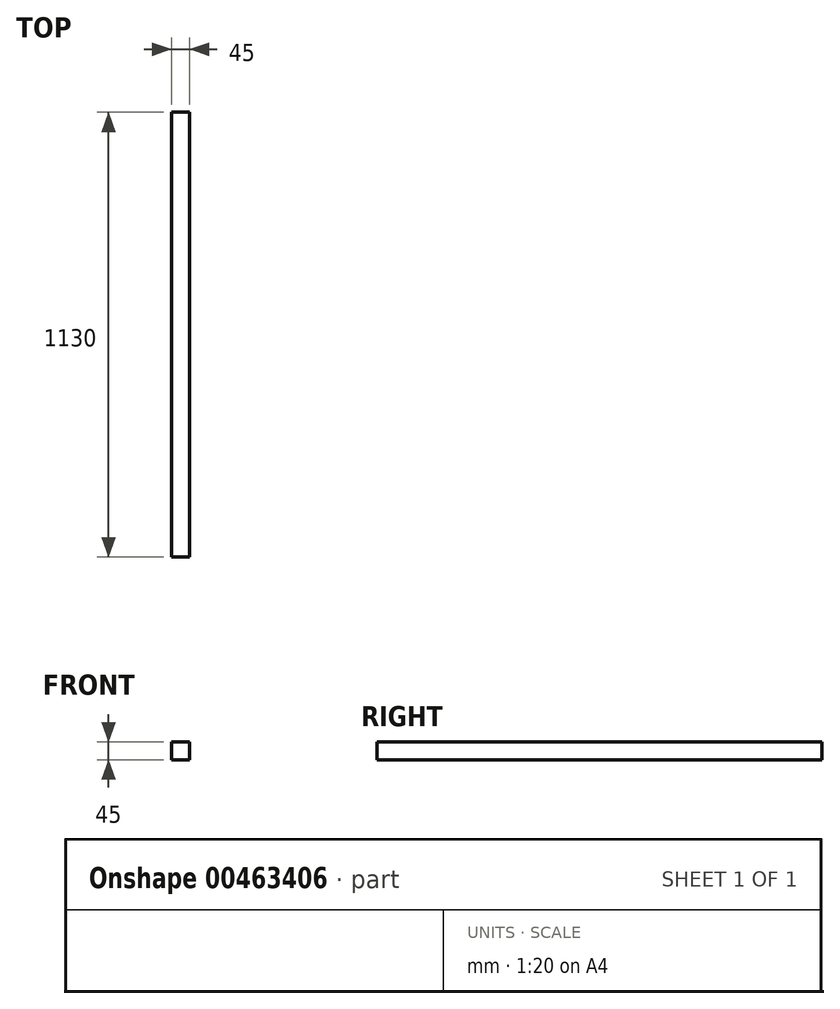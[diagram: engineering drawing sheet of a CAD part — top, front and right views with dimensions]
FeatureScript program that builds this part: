
annotation { "Feature Type Name" : "Feature", "Feature Type Description" : "" }
export const myFeature = defineFeature(function(context is Context, id is Id, definition is map)
    precondition{}
    {
        {
            var Q0;
            Q0=qCreatedBy(makeId("Front.planeOp"),FACE);
            var sketch = newSketch(context, id + "F0", { "sketchPlane" : qUnion([Q0])});
            skLineSegment(sketch, "E0.bottom", {"start": v(-45, 0) * mm, "end": v(0, 0) * mm});
            skLineSegment(sketch, "E0.top", {"start": v(-45, -45) * mm, "end": v(0, -45) * mm});
            skLineSegment(sketch, "E0.left", {"start": v(0, -45) * mm, "end": v(0, 0) * mm});
            skLineSegment(sketch, "E0.right", {"start": v(-45, -45) * mm, "end": v(-45, 0) * mm});
            skSolve(sketch);
        }
        {
            var Q0;
            Q0 = qSketchRegion(id + "F0", true);
            extrude(context, id + "F1", {"entities" : qUnion([Q0]), "depth" : 1130 * mm});
        }
    });
